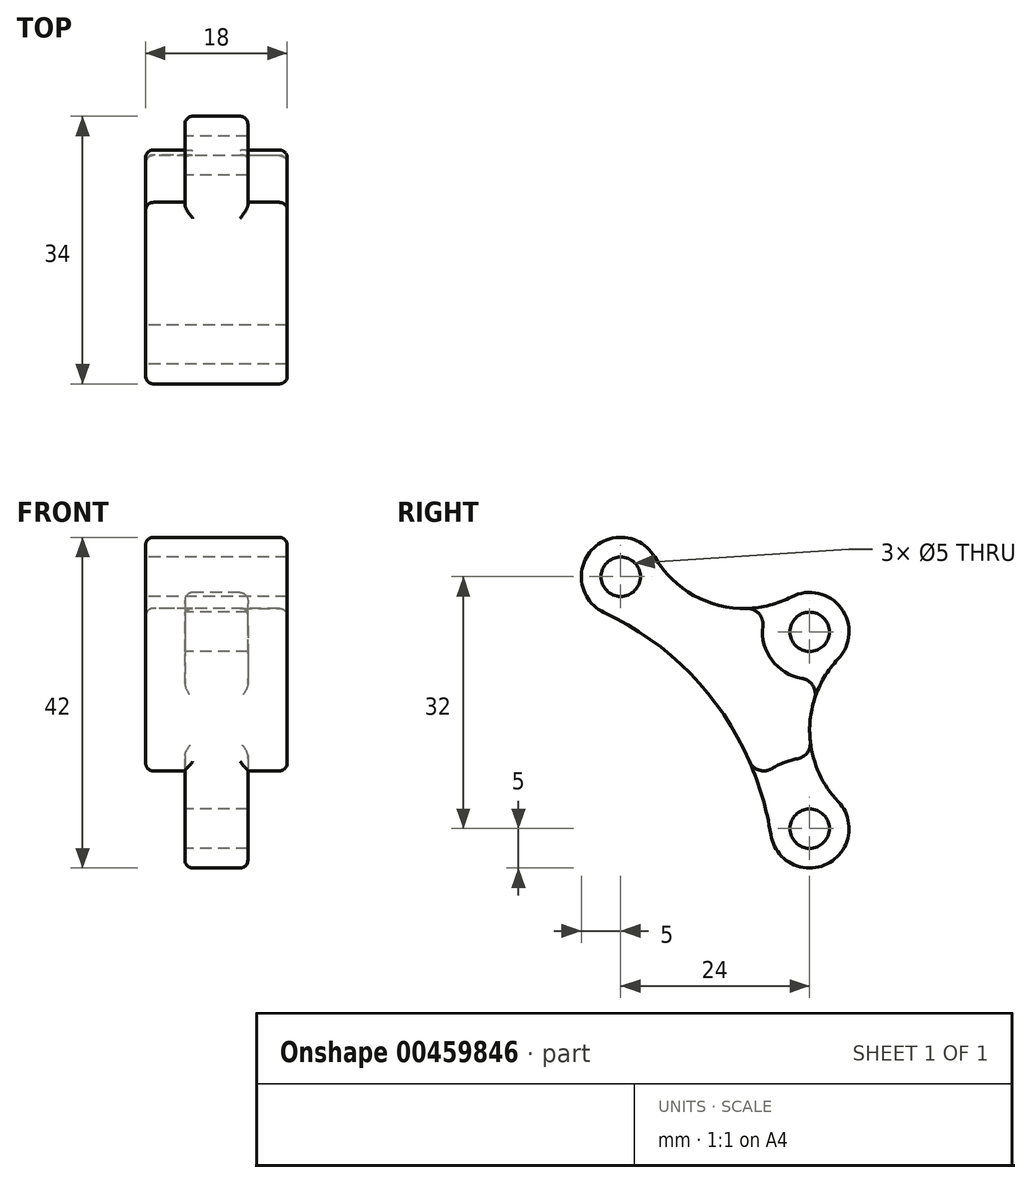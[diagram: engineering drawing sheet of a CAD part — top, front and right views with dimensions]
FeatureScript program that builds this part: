
annotation { "Feature Type Name" : "Feature", "Feature Type Description" : "" }
export const myFeature = defineFeature(function(context is Context, id is Id, definition is map)
    precondition{}
    {
        {
            var Q0;
            Q0=qCreatedBy(makeId("Right.planeOp"),FACE);
            var sketch = newSketch(context, id + "F0", { "sketchPlane" : qUnion([Q0])});
            skLineSegment(sketch, "E0", {"start": v(0, 0) * mm, "end": v(-24, 32) * mm});
            skLineSegment(sketch, "E1", {"start": v(-24, 32) * mm, "end": v(0, 25) * mm});
            skLineSegment(sketch, "E2", {"start": v(0, 25) * mm, "end": v(0, 0) * mm});
            skCircle(sketch, "E3", {"center": v(-24, 32) * mm, "radius": 2.5 * mm});
            skCircle(sketch, "E4", {"center": v(0, 25) * mm, "radius": 2.5 * mm});
            skCircle(sketch, "E5", {"center": v(0, 0) * mm, "radius": 2.5 * mm});
            skCircle(sketch, "E6", {"center": v(-24, 32) * mm, "radius": 5 * mm});
            skCircle(sketch, "E7", {"center": v(0, 25) * mm, "radius": 5 * mm});
            skCircle(sketch, "E8", {"center": v(0, 0) * mm, "radius": 5 * mm});
            skArc(sketch, "E9", {"start": v(-19.68, 34.51) * mm, "mid": v(-12, 28.5) * mm, "end": v(-2.3, 29.44) * mm});
            skArc(sketch, "E10", {"start": v(-4.94, -0.76) * mm, "mid": v(-12, 16) * mm, "end": v(-26.12, 27.47) * mm});
            skArc(sketch, "E11", {"start": v(3.62, 21.55) * mm, "mid": v(0, 12.5) * mm, "end": v(3.62, 3.45) * mm});
            skSolve(sketch);
        }
        {
            var Q0;
            {var subQ0=sQuery(id+"F0.wireOp",EDGE,"E10");var subQ1=sQuery(id+"F0.wireOp",EDGE,"E0");var subQ2=makeQuery(id+"F0.imprint","INTERSECT",VERTEX,{"derivedFrom":[subQ1,subQ0]});Q0=makeQuery(id+"F0.imprint","IMPRINT",FACE,{"disambiguationData":[TD([[makeQuery(id+"F0.imprint","IMPRINT",EDGE,{"disambiguationData":[TD([[subQ2,1.0]])],"derivedFrom":subQ1}),1.0]])]});}
            var Q1;
            {var subQ0=sQuery(id+"F0.wireOp",EDGE,"E10");var subQ1=sQuery(id+"F0.wireOp",EDGE,"E0");var subQ2=makeQuery(id+"F0.imprint","INTERSECT",VERTEX,{"derivedFrom":[subQ1,subQ0]});Q1=makeQuery(id+"F0.imprint","IMPRINT",FACE,{"disambiguationData":[TD([[makeQuery(id+"F0.imprint","IMPRINT",EDGE,{"disambiguationData":[TD([[subQ2,-1.0]])],"derivedFrom":subQ1}),1.0]])]});}
            var Q2;
            {var subQ0=sQuery(id+"F0.wireOp",EDGE,"E9");var subQ1=sQuery(id+"F0.wireOp",EDGE,"E1");var subQ2=makeQuery(id+"F0.imprint","INTERSECT",VERTEX,{"derivedFrom":[subQ1,subQ0]});Q2=makeQuery(id+"F0.imprint","IMPRINT",FACE,{"disambiguationData":[TD([[makeQuery(id+"F0.imprint","IMPRINT",EDGE,{"disambiguationData":[TD([[subQ2,1.0]])],"derivedFrom":subQ1}),1.0]])]});}
            var Q3;
            {var subQ0=sQuery(id+"F0.wireOp",EDGE,"E9");var subQ1=sQuery(id+"F0.wireOp",EDGE,"E1");var subQ2=makeQuery(id+"F0.imprint","INTERSECT",VERTEX,{"derivedFrom":[subQ1,subQ0]});Q3=makeQuery(id+"F0.imprint","IMPRINT",FACE,{"disambiguationData":[TD([[makeQuery(id+"F0.imprint","IMPRINT",EDGE,{"disambiguationData":[TD([[subQ2,-1.0]])],"derivedFrom":subQ1}),1.0]])]});}
            var Q4;
            {var subQ0=sQuery(id+"F0.wireOp",EDGE,"E11");var subQ1=sQuery(id+"F0.wireOp",EDGE,"E2");var subQ2=makeQuery(id+"F0.imprint","INTERSECT",VERTEX,{"derivedFrom":[subQ1,subQ0]});Q4=makeQuery(id+"F0.imprint","IMPRINT",FACE,{"disambiguationData":[TD([[makeQuery(id+"F0.imprint","IMPRINT",EDGE,{"disambiguationData":[TD([[subQ2,1.0]])],"derivedFrom":subQ1}),1.0]])]});}
            var Q5;
            {var subQ0=sQuery(id+"F0.wireOp",EDGE,"E11");var subQ1=sQuery(id+"F0.wireOp",EDGE,"E2");var subQ2=makeQuery(id+"F0.imprint","INTERSECT",VERTEX,{"derivedFrom":[subQ1,subQ0]});Q5=makeQuery(id+"F0.imprint","IMPRINT",FACE,{"disambiguationData":[TD([[makeQuery(id+"F0.imprint","IMPRINT",EDGE,{"disambiguationData":[TD([[subQ2,-1.0]])],"derivedFrom":subQ1}),1.0]])]});}
            var Q6;
            {var subQ4=sQuery(id+"F0.wireOp",EDGE,"E5");var subQ5=sQuery(id+"F0.wireOp",EDGE,"E0");var subQ6=makeQuery(id+"F0.imprint","INTERSECT",VERTEX,{"derivedFrom":[subQ5,subQ4]});Q6=makeQuery(id+"F0.imprint","IMPRINT",FACE,{"disambiguationData":[TD([[makeQuery(id+"F0.imprint","IMPRINT",EDGE,{"disambiguationData":[TD([[subQ6,-1.0]])],"derivedFrom":subQ5}),1.0]])]});}
            var Q7;
            {var subQ3=sQuery(id+"F0.wireOp",EDGE,"E6");var subQ6=sQuery(id+"F0.wireOp",EDGE,"E0");var subQ7=makeQuery(id+"F0.imprint","INTERSECT",VERTEX,{"derivedFrom":[subQ6,subQ3]});Q7=makeQuery(id+"F0.imprint","IMPRINT",FACE,{"disambiguationData":[TD([[makeQuery(id+"F0.imprint","IMPRINT",EDGE,{"disambiguationData":[TD([[subQ7,-1.0]])],"derivedFrom":subQ6}),1.0]])]});}
            var Q8;
            {var subQ1=sQuery(id+"F0.wireOp",EDGE,"E1");var subQ5=sQuery(id+"F0.wireOp",EDGE,"E7");var subQ6=makeQuery(id+"F0.imprint","INTERSECT",VERTEX,{"derivedFrom":[subQ1,subQ5]});Q8=makeQuery(id+"F0.imprint","IMPRINT",FACE,{"disambiguationData":[TD([[makeQuery(id+"F0.imprint","IMPRINT",EDGE,{"disambiguationData":[TD([[subQ6,-1.0]])],"derivedFrom":subQ1}),1.0]])]});}
            var Q9;
            {var subQ6=sQuery(id+"F0.wireOp",EDGE,"E0");var subQ7=makeQuery(id+"F0.imprint","INTERSECT",VERTEX,{"derivedFrom":[subQ6,sQuery(id+"F0.wireOp",EDGE,"E10")]});Q9=makeQuery(id+"F0.imprint","IMPRINT",FACE,{"disambiguationData":[TD([[makeQuery(id+"F0.imprint","IMPRINT",EDGE,{"disambiguationData":[TD([[subQ7,1.0]])],"derivedFrom":subQ6}),-1.0]])]});}
            var Q10;
            {var subQ0=sQuery(id+"F0.wireOp",EDGE,"E6");var subQ1=sQuery(id+"F0.wireOp",EDGE,"E0");var subQ2=makeQuery(id+"F0.imprint","INTERSECT",VERTEX,{"derivedFrom":[subQ1,subQ0]});Q10=makeQuery(id+"F0.imprint","IMPRINT",FACE,{"disambiguationData":[TD([[makeQuery(id+"F0.imprint","IMPRINT",EDGE,{"disambiguationData":[TD([[subQ2,-1.0]])],"derivedFrom":subQ1}),-1.0]])]});}
            var Q11;
            {var subQ0=sQuery(id+"F0.wireOp",EDGE,"E5");var subQ1=sQuery(id+"F0.wireOp",EDGE,"E0");var subQ2=makeQuery(id+"F0.imprint","INTERSECT",VERTEX,{"derivedFrom":[subQ1,subQ0]});Q11=makeQuery(id+"F0.imprint","IMPRINT",FACE,{"disambiguationData":[TD([[makeQuery(id+"F0.imprint","IMPRINT",EDGE,{"disambiguationData":[TD([[subQ2,-1.0]])],"derivedFrom":subQ1}),-1.0]])]});}
            var Q12;
            {var subQ0=sQuery(id+"F0.wireOp",EDGE,"E7");var subQ1=sQuery(id+"F0.wireOp",EDGE,"E1");var subQ2=makeQuery(id+"F0.imprint","INTERSECT",VERTEX,{"derivedFrom":[subQ1,subQ0]});Q12=makeQuery(id+"F0.imprint","IMPRINT",FACE,{"disambiguationData":[TD([[makeQuery(id+"F0.imprint","IMPRINT",EDGE,{"disambiguationData":[TD([[subQ2,-1.0]])],"derivedFrom":subQ1}),-1.0]])]});}
            extrude(context, id + "F1", {"entities" : qUnion([Q0, Q1, Q2, Q3, Q4, Q5, Q6, Q7, Q8, Q9, Q10, Q11, Q12]), "depth" : 9 * mm, "offsetDistance" : 25 * mm});
        }
        {
            var Q0;
            Q0=makeQuery(id+"F1.opExtrude","CAP_FACE",FACE,{"disambiguationData":[OSD([sQuery(id+"F0.wireOp",EDGE,"E3"),sQuery(id+"F0.wireOp",EDGE,"E4"),sQuery(id+"F0.wireOp",EDGE,"E5"),sQuery(id+"F0.wireOp",EDGE,"E6"),sQuery(id+"F0.wireOp",EDGE,"E7"),sQuery(id+"F0.wireOp",EDGE,"E8"),sQuery(id+"F0.wireOp",EDGE,"E9"),sQuery(id+"F0.wireOp",EDGE,"E10"),sQuery(id+"F0.wireOp",EDGE,"E11")])],"isStart":false});
            var sketch = newSketch(context, id + "F2", { "sketchPlane" : qUnion([Q0])});
            skCircle(sketch, "E12", {"center": v(0, 0) * mm, "radius": 9 * mm});
            skSolve(sketch);
        }
        {
            var Q0;
            Q0 = qSketchRegion(id + "F2", true);
            extrude(context, id + "F3", {"entities" : qUnion([Q0]), "operationType" : NewBodyOperationType.REMOVE, "oppositeDirection" : true, "depth" : 5 * mm, "offsetDistance" : 25 * mm});
        }
        {
            var Q0;
            Q0=makeQuery(id+"F1.opExtrude","CAP_FACE",FACE,{"disambiguationData":[OSD([sQuery(id+"F0.wireOp",EDGE,"E3"),sQuery(id+"F0.wireOp",EDGE,"E4"),sQuery(id+"F0.wireOp",EDGE,"E5"),sQuery(id+"F0.wireOp",EDGE,"E6"),sQuery(id+"F0.wireOp",EDGE,"E7"),sQuery(id+"F0.wireOp",EDGE,"E8"),sQuery(id+"F0.wireOp",EDGE,"E9"),sQuery(id+"F0.wireOp",EDGE,"E10"),sQuery(id+"F0.wireOp",EDGE,"E11")])],"isStart":false});
            var sketch = newSketch(context, id + "F4", { "sketchPlane" : qUnion([Q0])});
            skCircle(sketch, "E13", {"center": v(0, 25) * mm, "radius": 6 * mm});
            skSolve(sketch);
        }
        {
            var Q0;
            Q0 = qSketchRegion(id + "F4", true);
            extrude(context, id + "F5", {"entities" : qUnion([Q0]), "operationType" : NewBodyOperationType.REMOVE, "oppositeDirection" : true, "depth" : 5 * mm, "offsetDistance" : 25 * mm});
        }
        {
            var Q0;
            Q0=makeQuery(id+"F1.opExtrude","SWEPT_BODY",BODY,{"disambiguationData":[OSD([sQuery(id+"F0.wireOp",EDGE,"E3"),sQuery(id+"F0.wireOp",EDGE,"E4"),sQuery(id+"F0.wireOp",EDGE,"E5"),sQuery(id+"F0.wireOp",EDGE,"E6"),sQuery(id+"F0.wireOp",EDGE,"E7"),sQuery(id+"F0.wireOp",EDGE,"E8"),sQuery(id+"F0.wireOp",EDGE,"E9"),sQuery(id+"F0.wireOp",EDGE,"E10"),sQuery(id+"F0.wireOp",EDGE,"E11")])]});
            var Q1;
            Q1=makeQuery(id+"F1.opExtrude","CAP_FACE",FACE,{"disambiguationData":[OSD([sQuery(id+"F0.wireOp",EDGE,"E3"),sQuery(id+"F0.wireOp",EDGE,"E4"),sQuery(id+"F0.wireOp",EDGE,"E5"),sQuery(id+"F0.wireOp",EDGE,"E6"),sQuery(id+"F0.wireOp",EDGE,"E7"),sQuery(id+"F0.wireOp",EDGE,"E8"),sQuery(id+"F0.wireOp",EDGE,"E9"),sQuery(id+"F0.wireOp",EDGE,"E10"),sQuery(id+"F0.wireOp",EDGE,"E11")])],"isStart":true});
            mirror(context, id + "F6", {"operationType" : NewBodyOperationType.ADD, "entities" : qUnion([Q0]), "mirrorPlane" : qUnion([Q1])});
        }
        {
            var Q0;
            Q0=makeQuery(id+"F6.opPattern","COPY",EDGE,{"derivedFrom":makeQuery(id+"F5.boolean.opBoolean","INTERSECT",EDGE,{"derivedFrom":[makeQuery(id+"F1.opExtrude","SWEPT_FACE",FACE,{"disambiguationData":[OSD([sQuery(id+"F0.wireOp",EDGE,"E9")])]}),makeQuery(id+"F5.opExtrude","SWEPT_FACE",FACE,{"disambiguationData":[OSD([sQuery(id+"F4.wireOp",EDGE,"E13")])]})]}),"instanceName":"1"});
            var Q1;
            Q1=makeQuery(id+"F6.opPattern","COPY",EDGE,{"derivedFrom":makeQuery(id+"F5.boolean.opBoolean","INTERSECT",EDGE,{"derivedFrom":[makeQuery(id+"F1.opExtrude","SWEPT_FACE",FACE,{"disambiguationData":[OSD([sQuery(id+"F0.wireOp",EDGE,"E11")])]}),makeQuery(id+"F5.opExtrude","SWEPT_FACE",FACE,{"disambiguationData":[OSD([sQuery(id+"F4.wireOp",EDGE,"E13")])]})]}),"instanceName":"1"});
            var Q2;
            Q2=makeQuery(id+"F5.boolean.opBoolean","INTERSECT",EDGE,{"derivedFrom":[makeQuery(id+"F1.opExtrude","SWEPT_FACE",FACE,{"disambiguationData":[OSD([sQuery(id+"F0.wireOp",EDGE,"E11")])]}),makeQuery(id+"F5.opExtrude","SWEPT_FACE",FACE,{"disambiguationData":[OSD([sQuery(id+"F4.wireOp",EDGE,"E13")])]})]});
            var Q3;
            Q3=makeQuery(id+"F5.boolean.opBoolean","INTERSECT",EDGE,{"derivedFrom":[makeQuery(id+"F1.opExtrude","SWEPT_FACE",FACE,{"disambiguationData":[OSD([sQuery(id+"F0.wireOp",EDGE,"E9")])]}),makeQuery(id+"F5.opExtrude","SWEPT_FACE",FACE,{"disambiguationData":[OSD([sQuery(id+"F4.wireOp",EDGE,"E13")])]})]});
            var Q4;
            Q4=makeQuery(id+"F6.opPattern","COPY",EDGE,{"derivedFrom":makeQuery(id+"F3.boolean.opBoolean","INTERSECT",EDGE,{"derivedFrom":[makeQuery(id+"F1.opExtrude","SWEPT_FACE",FACE,{"disambiguationData":[OSD([sQuery(id+"F0.wireOp",EDGE,"E11")])]}),makeQuery(id+"F3.opExtrude","SWEPT_FACE",FACE,{"disambiguationData":[OSD([sQuery(id+"F2.wireOp",EDGE,"E12")])]})]}),"instanceName":"1"});
            var Q5;
            Q5=makeQuery(id+"F6.opPattern","COPY",EDGE,{"derivedFrom":makeQuery(id+"F3.boolean.opBoolean","INTERSECT",EDGE,{"derivedFrom":[makeQuery(id+"F1.opExtrude","SWEPT_FACE",FACE,{"disambiguationData":[OSD([sQuery(id+"F0.wireOp",EDGE,"E10")])]}),makeQuery(id+"F3.opExtrude","SWEPT_FACE",FACE,{"disambiguationData":[OSD([sQuery(id+"F2.wireOp",EDGE,"E12")])]})]}),"instanceName":"1"});
            var Q6;
            Q6=makeQuery(id+"F3.boolean.opBoolean","INTERSECT",EDGE,{"derivedFrom":[makeQuery(id+"F1.opExtrude","SWEPT_FACE",FACE,{"disambiguationData":[OSD([sQuery(id+"F0.wireOp",EDGE,"E10")])]}),makeQuery(id+"F3.opExtrude","SWEPT_FACE",FACE,{"disambiguationData":[OSD([sQuery(id+"F2.wireOp",EDGE,"E12")])]})]});
            var Q7;
            Q7=makeQuery(id+"F3.boolean.opBoolean","INTERSECT",EDGE,{"derivedFrom":[makeQuery(id+"F1.opExtrude","SWEPT_FACE",FACE,{"disambiguationData":[OSD([sQuery(id+"F0.wireOp",EDGE,"E11")])]}),makeQuery(id+"F3.opExtrude","SWEPT_FACE",FACE,{"disambiguationData":[OSD([sQuery(id+"F2.wireOp",EDGE,"E12")])]})]});
            fillet(context, id + "F7", {"entities" : qUnion([Q0, Q1, Q2, Q3, Q4, Q5, Q6, Q7]), "radius" : 2 * mm, "tangentPropagation" : true, "allowEdgeOverflow" : false});
        }
        {
            var Q0;
            Q0=makeQuery(id+"F1.opExtrude","CAP_EDGE",EDGE,{"disambiguationData":[OSD([sQuery(id+"F0.wireOp",EDGE,"E9")])],"isStart":false});
            var Q1;
            Q1=makeQuery(id+"F6.opPattern","COPY",EDGE,{"derivedFrom":makeQuery(id+"F1.opExtrude","CAP_EDGE",EDGE,{"disambiguationData":[OSD([sQuery(id+"F0.wireOp",EDGE,"E11")])],"isStart":false}),"instanceName":"1"});
            var Q2;
            Q2=makeQuery(id+"F6.opPattern","COPY",EDGE,{"derivedFrom":makeQuery(id+"F5.boolean.opBoolean","INTERSECT",EDGE,{"derivedFrom":[makeQuery(id+"F1.opExtrude","SWEPT_FACE",FACE,{"disambiguationData":[OSD([sQuery(id+"F0.wireOp",EDGE,"E7")])]}),makeQuery(id+"F5.opExtrude","CAP_FACE",FACE,{"disambiguationData":[OSD([sQuery(id+"F4.wireOp",EDGE,"E13")])],"isStart":false})]}),"instanceName":"1"});
            var Q3;
            Q3=makeQuery(id+"F6.opPattern","COPY",EDGE,{"derivedFrom":makeQuery(id+"F3.boolean.opBoolean","INTERSECT",EDGE,{"derivedFrom":[makeQuery(id+"F1.opExtrude","SWEPT_FACE",FACE,{"disambiguationData":[OSD([sQuery(id+"F0.wireOp",EDGE,"E11")])]}),makeQuery(id+"F3.opExtrude","CAP_FACE",FACE,{"disambiguationData":[OSD([sQuery(id+"F2.wireOp",EDGE,"E12")])],"isStart":false})]}),"instanceName":"1"});
            var Q4;
            Q4=makeQuery(id+"F3.boolean.opBoolean","INTERSECT",EDGE,{"derivedFrom":[makeQuery(id+"F1.opExtrude","SWEPT_FACE",FACE,{"disambiguationData":[OSD([sQuery(id+"F0.wireOp",EDGE,"E11")])]}),makeQuery(id+"F3.opExtrude","CAP_FACE",FACE,{"disambiguationData":[OSD([sQuery(id+"F2.wireOp",EDGE,"E12")])],"isStart":false})]});
            var Q5;
            Q5=makeQuery(id+"F5.boolean.opBoolean","INTERSECT",EDGE,{"derivedFrom":[makeQuery(id+"F1.opExtrude","SWEPT_FACE",FACE,{"disambiguationData":[OSD([sQuery(id+"F0.wireOp",EDGE,"E11")])]}),makeQuery(id+"F5.opExtrude","CAP_FACE",FACE,{"disambiguationData":[OSD([sQuery(id+"F4.wireOp",EDGE,"E13")])],"isStart":false})]});
            fillet(context, id + "F8", {"entities" : qUnion([Q0, Q1, Q2, Q3, Q4, Q5]), "radius" : 1 * mm, "tangentPropagation" : true, "allowEdgeOverflow" : false});
        }
    });
